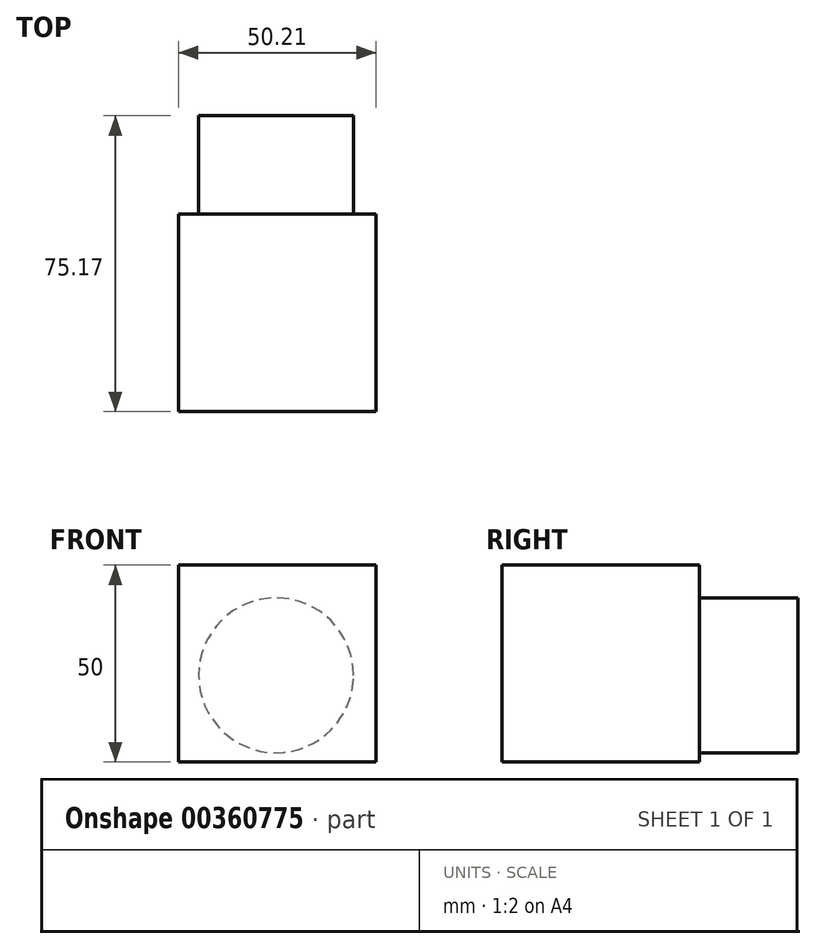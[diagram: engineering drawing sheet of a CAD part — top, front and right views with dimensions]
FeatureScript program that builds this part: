
annotation { "Feature Type Name" : "Feature", "Feature Type Description" : "" }
export const myFeature = defineFeature(function(context is Context, id is Id, definition is map)
    precondition{}
    {
        {
            var Q0;
            Q0=qCreatedBy(makeId("Top.planeOp"),FACE);
            var sketch = newSketch(context, id + "F0", { "sketchPlane" : qUnion([Q0])});
            skLineSegment(sketch, "E0.bottom", {"start": v(0, 0) * mm, "end": v(50.21, 0) * mm});
            skLineSegment(sketch, "E0.top", {"start": v(0, 50.17) * mm, "end": v(50.21, 50.17) * mm});
            skLineSegment(sketch, "E0.left", {"start": v(0, 0) * mm, "end": v(0, 50.17) * mm});
            skLineSegment(sketch, "E0.right", {"start": v(50.21, 0) * mm, "end": v(50.21, 50.17) * mm});
            skSolve(sketch);
        }
        {
            var Q0;
            Q0 = qSketchRegion(id + "F0", true);
            extrude(context, id + "F1", {"entities" : qUnion([Q0]), "depth" : 50 * mm});
        }
        {
            var Q0;
            Q0=makeQuery(id+"F1.opExtrude","SWEPT_FACE",FACE,{"disambiguationData":[OSD([sQuery(id+"F0.wireOp",EDGE,"E0.top")])]});
            var sketch = newSketch(context, id + "F2", { "sketchPlane" : qUnion([Q0])});
            skCircle(sketch, "E1", {"center": v(-24.82, 21.98) * mm, "radius": 19.67 * mm});
            skSolve(sketch);
        }
        {
            var Q0;
            Q0 = qSketchRegion(id + "F2", true);
            extrude(context, id + "F3", {"entities" : qUnion([Q0]), "operationType" : NewBodyOperationType.ADD, "depth" : 25 * mm});
        }
    });
